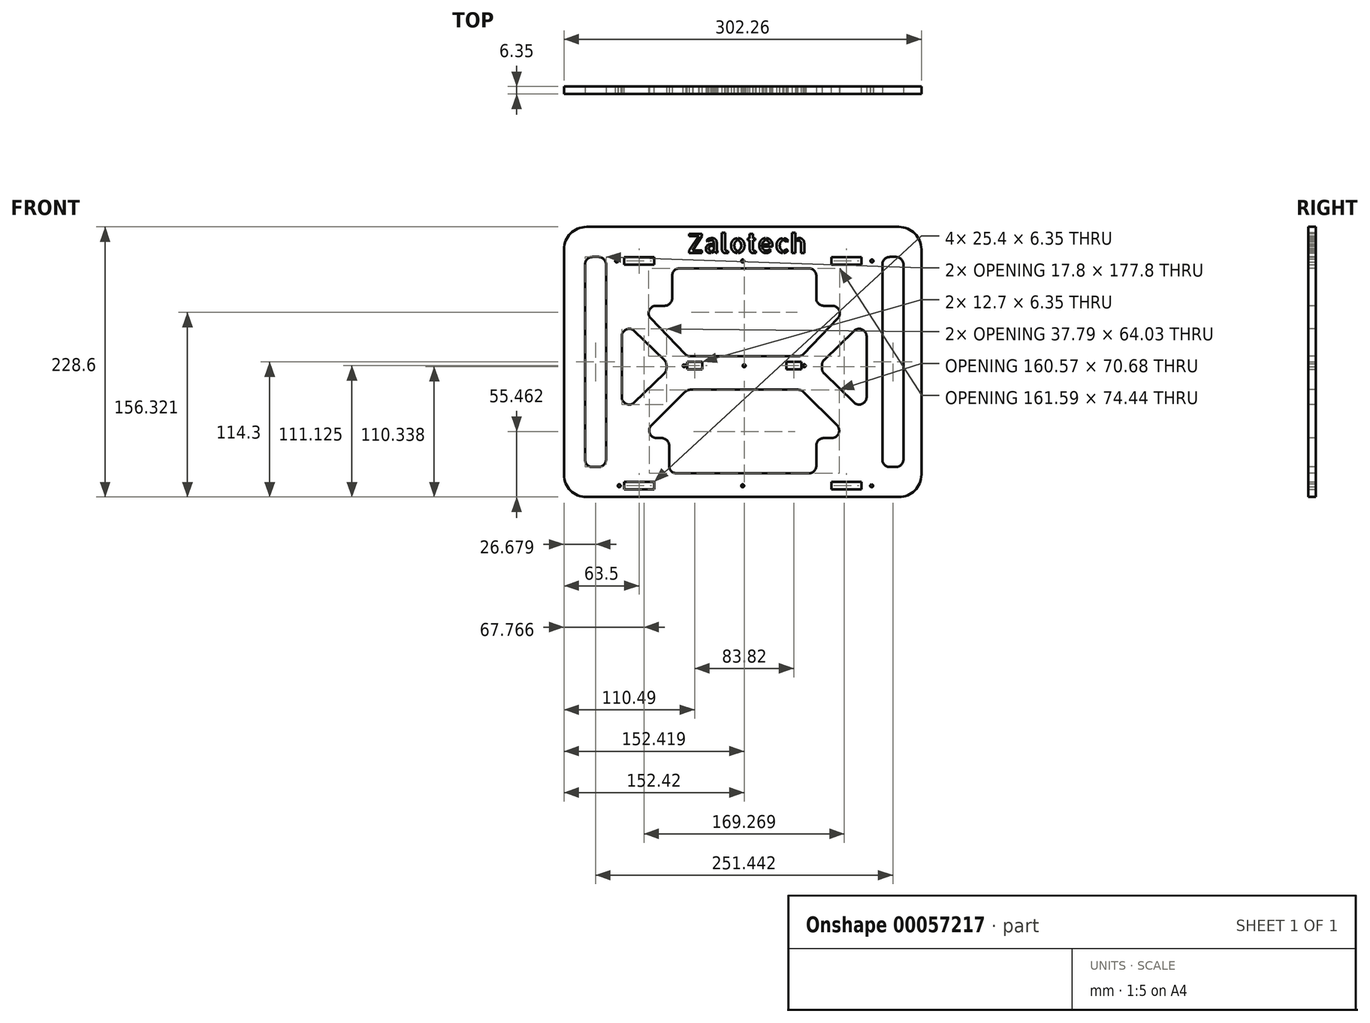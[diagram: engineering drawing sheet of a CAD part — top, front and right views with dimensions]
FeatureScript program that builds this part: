
annotation { "Feature Type Name" : "Feature", "Feature Type Description" : "" }
export const myFeature = defineFeature(function(context is Context, id is Id, definition is map)
    precondition{}
    {
        {
            var Q0;
            Q0=qCreatedBy(makeId("Front.planeOp"),FACE);
            var sketch = newSketch(context, id + "F0", { "sketchPlane" : qUnion([Q0])});
            skLineSegment(sketch, "E0.bottom", {"start": v(-133.35, 114.3) * mm, "end": v(130.8, 114.3) * mm});
            skLineSegment(sketch, "E0.top", {"start": v(-133.35, -114.3) * mm, "end": v(130.8, -114.3) * mm});
            skLineSegment(sketch, "E0.left", {"start": v(-152.4, 95.25) * mm, "end": v(-152.4, -95.25) * mm});
            skLineSegment(sketch, "E0.right", {"start": v(149.86, 95.25) * mm, "end": v(149.86, -95.25) * mm});
            skLineSegment(sketch, "E1", {"start": v(-152.4, -101.6) * mm, "end": v(-101.6, -101.6) * mm, "construction": true});
            skLineSegment(sketch, "E2", {"start": v(149.86, -101.6) * mm, "end": v(99.06, -101.6) * mm, "construction": true});
            skLineSegment(sketch, "E3", {"start": v(-101.6, -101.6) * mm, "end": v(-101.6, -114.3) * mm, "construction": true});
            skLineSegment(sketch, "E4", {"start": v(99.06, -101.6) * mm, "end": v(99.06, -114.3) * mm, "construction": true});
            skPoint(sketch, "E5.oppositeSnap0", {"position": v(-101.6, -107.95) * mm});
            skLineSegment(sketch, "E5.bottom", {"start": v(-101.6, -101.6) * mm, "end": v(-76.2, -101.6) * mm});
            skLineSegment(sketch, "E5.top", {"start": v(-101.6, -107.95) * mm, "end": v(-76.2, -107.95) * mm});
            skLineSegment(sketch, "E5.left", {"start": v(-101.6, -101.6) * mm, "end": v(-101.6, -107.95) * mm});
            skLineSegment(sketch, "E5.right", {"start": v(-76.2, -101.6) * mm, "end": v(-76.2, -107.95) * mm});
            skLineSegment(sketch, "E6.bottom", {"start": v(99.06, -101.6) * mm, "end": v(73.66, -101.6) * mm});
            skLineSegment(sketch, "E6.top", {"start": v(99.06, -107.95) * mm, "end": v(73.66, -107.95) * mm});
            skLineSegment(sketch, "E6.left", {"start": v(99.06, -101.6) * mm, "end": v(99.06, -107.95) * mm});
            skLineSegment(sketch, "E6.right", {"start": v(73.66, -101.6) * mm, "end": v(73.66, -107.95) * mm});
            skLineSegment(sketch, "E7", {"start": v(48.26, 0) * mm, "end": v(-48.26, 0) * mm, "construction": true});
            skLineSegment(sketch, "E8.bottom", {"start": v(48.26, 0) * mm, "end": v(35.56, 0) * mm});
            skLineSegment(sketch, "E8.top", {"start": v(48.26, -6.35) * mm, "end": v(35.56, -6.35) * mm});
            skLineSegment(sketch, "E8.left", {"start": v(48.26, 0) * mm, "end": v(48.26, -6.35) * mm});
            skLineSegment(sketch, "E8.right", {"start": v(35.56, 0) * mm, "end": v(35.56, -6.35) * mm});
            skLineSegment(sketch, "E9.bottom", {"start": v(-48.26, 0) * mm, "end": v(-35.56, 0) * mm});
            skLineSegment(sketch, "E9.top", {"start": v(-48.26, -6.35) * mm, "end": v(-35.56, -6.35) * mm});
            skLineSegment(sketch, "E9.left", {"start": v(-48.26, 0) * mm, "end": v(-48.26, -6.35) * mm});
            skLineSegment(sketch, "E9.right", {"start": v(-35.56, 0) * mm, "end": v(-35.56, -6.35) * mm});
            skLineSegment(sketch, "E10", {"start": v(-101.6, -101.6) * mm, "end": v(-101.6, 88.67) * mm, "construction": true});
            skLineSegment(sketch, "E11", {"start": v(-76.2, -101.6) * mm, "end": v(-76.2, 88.67) * mm, "construction": true});
            skLineSegment(sketch, "E12", {"start": v(-101.6, 88.67) * mm, "end": v(-76.2, 88.67) * mm, "construction": true});
            skLineSegment(sketch, "E13", {"start": v(-101.6, 88.67) * mm, "end": v(108.78, 88.67) * mm, "construction": true});
            skLineSegment(sketch, "E14", {"start": v(99.06, -101.6) * mm, "end": v(99.06, 88.67) * mm, "construction": true});
            skLineSegment(sketch, "E15", {"start": v(73.66, -101.6) * mm, "end": v(73.66, 88.67) * mm, "construction": true});
            skLineSegment(sketch, "E16.bottom", {"start": v(-101.6, 88.67) * mm, "end": v(-76.2, 88.67) * mm});
            skLineSegment(sketch, "E16.top", {"start": v(-101.6, 82.32) * mm, "end": v(-76.2, 82.32) * mm});
            skLineSegment(sketch, "E16.left", {"start": v(-101.6, 88.67) * mm, "end": v(-101.6, 82.32) * mm});
            skLineSegment(sketch, "E16.right", {"start": v(-76.2, 88.67) * mm, "end": v(-76.2, 82.32) * mm});
            skLineSegment(sketch, "E17.bottom", {"start": v(73.66, 88.67) * mm, "end": v(99.06, 88.67) * mm});
            skLineSegment(sketch, "E17.top", {"start": v(73.66, 82.32) * mm, "end": v(99.06, 82.32) * mm});
            skLineSegment(sketch, "E17.left", {"start": v(73.66, 88.67) * mm, "end": v(73.66, 82.32) * mm});
            skLineSegment(sketch, "E17.right", {"start": v(99.06, 88.67) * mm, "end": v(99.06, 82.32) * mm});
            skPoint(sketch, "E18.visualSharp", {"position": v(-152.4, 114.3) * mm});
            skArc(sketch, "E18.filletArc", {"start": v(-133.35, 114.3) * mm, "mid": v(-146.82, 108.72) * mm, "end": v(-152.4, 95.25) * mm});
            skPoint(sketch, "E19.visualSharp", {"position": v(149.86, 114.3) * mm});
            skArc(sketch, "E19.filletArc", {"start": v(149.86, 95.25) * mm, "mid": v(144.28, 108.72) * mm, "end": v(130.8, 114.3) * mm});
            skPoint(sketch, "E20.visualSharp", {"position": v(149.86, -114.3) * mm});
            skArc(sketch, "E20.filletArc", {"start": v(130.8, -114.3) * mm, "mid": v(144.28, -108.72) * mm, "end": v(149.86, -95.25) * mm});
            skPoint(sketch, "E21.visualSharp", {"position": v(-152.4, -114.3) * mm});
            skArc(sketch, "E21.filletArc", {"start": v(-152.4, -95.25) * mm, "mid": v(-146.82, -108.72) * mm, "end": v(-133.35, -114.3) * mm});
            skSolve(sketch);
        }
        {
            var Q0;
            Q0=makeQuery(id+"F0.imprint","IMPRINT",FACE,{"disambiguationData":[TD([[makeQuery(id+"F0.imprint","IMPRINT",EDGE,{"derivedFrom":sQuery(id+"F0.wireOp",EDGE,"E0.bottom")}),-1.0]])]});
            extrude(context, id + "F1", {"entities" : qUnion([Q0]), "depth" : 6.35 * mm});
        }
        {
            var Q0;
            Q0=makeQuery(id+"F1.opExtrude","CAP_FACE",FACE,{"disambiguationData":[OSD([sQuery(id+"F0.wireOp",EDGE,"E0.bottom"),sQuery(id+"F0.wireOp",EDGE,"E0.top"),sQuery(id+"F0.wireOp",EDGE,"E0.left"),sQuery(id+"F0.wireOp",EDGE,"E0.right"),sQuery(id+"F0.wireOp",EDGE,"E5.bottom"),sQuery(id+"F0.wireOp",EDGE,"E5.top"),sQuery(id+"F0.wireOp",EDGE,"E5.left"),sQuery(id+"F0.wireOp",EDGE,"E5.right"),sQuery(id+"F0.wireOp",EDGE,"E6.bottom"),sQuery(id+"F0.wireOp",EDGE,"E6.top"),sQuery(id+"F0.wireOp",EDGE,"E6.left"),sQuery(id+"F0.wireOp",EDGE,"E6.right"),sQuery(id+"F0.wireOp",EDGE,"E8.bottom"),sQuery(id+"F0.wireOp",EDGE,"E8.top"),sQuery(id+"F0.wireOp",EDGE,"E8.left"),sQuery(id+"F0.wireOp",EDGE,"E8.right"),sQuery(id+"F0.wireOp",EDGE,"E9.bottom"),sQuery(id+"F0.wireOp",EDGE,"E9.top"),sQuery(id+"F0.wireOp",EDGE,"E9.left"),sQuery(id+"F0.wireOp",EDGE,"E9.right"),sQuery(id+"F0.wireOp",EDGE,"E16.bottom"),sQuery(id+"F0.wireOp",EDGE,"E16.top"),sQuery(id+"F0.wireOp",EDGE,"E16.left"),sQuery(id+"F0.wireOp",EDGE,"E16.right"),sQuery(id+"F0.wireOp",EDGE,"E17.bottom"),sQuery(id+"F0.wireOp",EDGE,"E17.top"),sQuery(id+"F0.wireOp",EDGE,"E17.left"),sQuery(id+"F0.wireOp",EDGE,"E17.right")])],"isStart":false});
            var sketch = newSketch(context, id + "F2", { "sketchPlane" : qUnion([Q0])});
            skLineSegment(sketch, "E22", {"start": v(-63.5, -77.67) * mm, "end": v(-63.5, -87.83) * mm});
            skLineSegment(sketch, "E23", {"start": v(-57.15, -94.18) * mm, "end": v(54.6, -94.18) * mm});
            skLineSegment(sketch, "E24", {"start": v(60.96, -87.83) * mm, "end": v(60.96, -77.67) * mm});
            skLineSegment(sketch, "E25", {"start": v(-54.6, 79.24) * mm, "end": v(54.6, 79.24) * mm});
            skLineSegment(sketch, "E26", {"start": v(-45.5, 4.8) * mm, "end": v(45.66, 4.8) * mm});
            skLineSegment(sketch, "E27", {"start": v(74.5, 47.62) * mm, "end": v(67.18, 47.62) * mm});
            skLineSegment(sketch, "E28.MirrorCS", {"start": v(-74.47, 47.62) * mm, "end": v(-67.18, 47.62) * mm});
            skLineSegment(sketch, "E29", {"start": v(-50.09, 6.75) * mm, "end": v(-79.04, 36.87) * mm});
            skLineSegment(sketch, "E30", {"start": v(50.24, 6.76) * mm, "end": v(79.1, 36.88) * mm});
            skLineSegment(sketch, "E31", {"start": v(-60.96, 53.84) * mm, "end": v(-60.96, 72.9) * mm});
            skLineSegment(sketch, "E32", {"start": v(60.96, 53.84) * mm, "end": v(60.96, 72.9) * mm});
            skLineSegment(sketch, "E33", {"start": v(-45.5, -23.5) * mm, "end": v(45.66, -23.5) * mm});
            skLineSegment(sketch, "E34", {"start": v(89.38, 47.62) * mm, "end": v(89.38, -82.33) * mm, "construction": true});
            skLineSegment(sketch, "E35", {"start": v(60.96, 47.62) * mm, "end": v(-60.96, 47.62) * mm, "construction": true});
            skLineSegment(sketch, "E36", {"start": v(-78.41, -53.5) * mm, "end": v(-49.98, -25.33) * mm});
            skLineSegment(sketch, "E37", {"start": v(50.14, -25.34) * mm, "end": v(78.46, -53.51) * mm});
            skLineSegment(sketch, "E38", {"start": v(-63.5, -77.67) * mm, "end": v(-63.5, -70.71) * mm});
            skLineSegment(sketch, "E39", {"start": v(60.96, -77.67) * mm, "end": v(60.96, -70.71) * mm});
            skLineSegment(sketch, "E40", {"start": v(73.99, -64.36) * mm, "end": v(67.3, -64.36) * mm});
            skLineSegment(sketch, "E41", {"start": v(-69.85, -64.36) * mm, "end": v(-73.95, -64.36) * mm});
            skArc(sketch, "E42.filletArc", {"start": v(-74.47, 47.62) * mm, "mid": v(-80.3, 43.76) * mm, "end": v(-79.04, 36.87) * mm});
            skPoint(sketch, "E43.visualSharp", {"position": v(89.38, 47.62) * mm});
            skArc(sketch, "E43.filletArc", {"start": v(79.1, 36.88) * mm, "mid": v(80.34, 43.76) * mm, "end": v(74.5, 47.62) * mm});
            skPoint(sketch, "E44.visualSharp", {"position": v(48.37, 4.8) * mm});
            skArc(sketch, "E44.filletArc", {"start": v(45.66, 4.8) * mm, "mid": v(48.15, 5.3) * mm, "end": v(50.24, 6.76) * mm});
            skPoint(sketch, "E45.visualSharp", {"position": v(-48.21, 4.8) * mm});
            skArc(sketch, "E45.filletArc", {"start": v(-50.09, 6.75) * mm, "mid": v(-48, 5.3) * mm, "end": v(-45.5, 4.8) * mm});
            skPoint(sketch, "E46.visualSharp", {"position": v(-48.12, -23.5) * mm});
            skArc(sketch, "E46.filletArc", {"start": v(-45.5, -23.5) * mm, "mid": v(-47.92, -23.97) * mm, "end": v(-49.98, -25.33) * mm});
            skPoint(sketch, "E47.visualSharp", {"position": v(48.28, -23.5) * mm});
            skArc(sketch, "E47.filletArc", {"start": v(50.14, -25.34) * mm, "mid": v(48.08, -23.97) * mm, "end": v(45.66, -23.5) * mm});
            skPoint(sketch, "E48.visualSharp", {"position": v(89.38, -64.36) * mm});
            skArc(sketch, "E48.filletArc", {"start": v(73.99, -64.36) * mm, "mid": v(79.86, -60.44) * mm, "end": v(78.46, -53.51) * mm});
            skArc(sketch, "E49.filletArc", {"start": v(-78.41, -53.5) * mm, "mid": v(-79.82, -60.43) * mm, "end": v(-73.95, -64.36) * mm});
            skPoint(sketch, "E50.visualSharp", {"position": v(-63.5, -64.36) * mm});
            skArc(sketch, "E50.filletArc", {"start": v(-63.5, -70.71) * mm, "mid": v(-65.36, -66.22) * mm, "end": v(-69.85, -64.36) * mm});
            skPoint(sketch, "E51.visualSharp", {"position": v(60.96, -64.36) * mm});
            skArc(sketch, "E51.filletArc", {"start": v(67.3, -64.36) * mm, "mid": v(62.82, -66.22) * mm, "end": v(60.96, -70.71) * mm});
            skArc(sketch, "E52.filletArc", {"start": v(-67.18, 47.62) * mm, "mid": v(-62.78, 49.44) * mm, "end": v(-60.96, 53.84) * mm});
            skArc(sketch, "E53.filletArc", {"start": v(60.96, 53.84) * mm, "mid": v(62.78, 49.44) * mm, "end": v(67.18, 47.62) * mm});
            skArc(sketch, "E54.filletArc", {"start": v(-54.6, 79.24) * mm, "mid": v(-59.1, 77.38) * mm, "end": v(-60.96, 72.9) * mm});
            skArc(sketch, "E55.filletArc", {"start": v(60.96, 72.9) * mm, "mid": v(59.1, 77.38) * mm, "end": v(54.6, 79.24) * mm});
            skPoint(sketch, "E56.visualSharp", {"position": v(-63.5, -94.18) * mm});
            skArc(sketch, "E56.filletArc", {"start": v(-63.5, -87.83) * mm, "mid": v(-61.64, -92.32) * mm, "end": v(-57.15, -94.18) * mm});
            skPoint(sketch, "E57.visualSharp", {"position": v(60.96, -94.18) * mm});
            skArc(sketch, "E57.filletArc", {"start": v(54.6, -94.18) * mm, "mid": v(59.1, -92.32) * mm, "end": v(60.96, -87.83) * mm});
            skSolve(sketch);
        }
        {
            var Q0;
            Q0=makeQuery(id+"F2.imprint","IMPRINT",FACE,{"disambiguationData":[TD([[makeQuery(id+"F2.imprint","IMPRINT",EDGE,{"derivedFrom":sQuery(id+"F2.wireOp",EDGE,"E26")}),1.0]])]});
            var Q1;
            {var subQ3=sQuery(id+"F2.wireOp",EDGE,"E23");Q1=makeQuery(id+"F2.imprint","IMPRINT",FACE,{"disambiguationData":[TD([[makeQuery(id+"F2.imprint","IMPRINT",EDGE,{"derivedFrom":subQ3}),1.0]])]});}
            var Q2;
            Q2=makeQuery(id+"F2.imprint","IMPRINT",FACE,{"disambiguationData":[TD([[makeQuery(id+"F2.imprint","IMPRINT",EDGE,{"derivedFrom":sQuery(id+"F2.wireOp",EDGE,"f44173c2-0543-4982-a62a-dc314a2ca8c5")}),-1.0]])]});
            var Q3;
            Q3=makeQuery(id+"F2.imprint","IMPRINT",FACE,{"disambiguationData":[TD([[makeQuery(id+"F2.imprint","IMPRINT",EDGE,{"derivedFrom":sQuery(id+"F2.wireOp",EDGE,"1ee7fdb6-237e-4fa8-abf3-a4b38ba9088a0.MirrorCS")}),1.0]])]});
            extrude(context, id + "F3", {"entities" : qUnion([Q0, Q1, Q2, Q3]), "operationType" : NewBodyOperationType.REMOVE, "oppositeDirection" : true, "depth" : 25.4 * mm});
        }
        {
            var Q0;
            Q0=makeQuery(id+"F1.opExtrude","CAP_FACE",FACE,{"disambiguationData":[OSD([sQuery(id+"F0.wireOp",EDGE,"E0.bottom"),sQuery(id+"F0.wireOp",EDGE,"E0.top"),sQuery(id+"F0.wireOp",EDGE,"E0.left"),sQuery(id+"F0.wireOp",EDGE,"E0.right"),sQuery(id+"F0.wireOp",EDGE,"E5.bottom"),sQuery(id+"F0.wireOp",EDGE,"E5.top"),sQuery(id+"F0.wireOp",EDGE,"E5.left"),sQuery(id+"F0.wireOp",EDGE,"E5.right"),sQuery(id+"F0.wireOp",EDGE,"E6.bottom"),sQuery(id+"F0.wireOp",EDGE,"E6.top"),sQuery(id+"F0.wireOp",EDGE,"E6.left"),sQuery(id+"F0.wireOp",EDGE,"E6.right"),sQuery(id+"F0.wireOp",EDGE,"E8.bottom"),sQuery(id+"F0.wireOp",EDGE,"E8.top"),sQuery(id+"F0.wireOp",EDGE,"E8.left"),sQuery(id+"F0.wireOp",EDGE,"E8.right"),sQuery(id+"F0.wireOp",EDGE,"E9.bottom"),sQuery(id+"F0.wireOp",EDGE,"E9.top"),sQuery(id+"F0.wireOp",EDGE,"E9.left"),sQuery(id+"F0.wireOp",EDGE,"E9.right"),sQuery(id+"F0.wireOp",EDGE,"E16.bottom"),sQuery(id+"F0.wireOp",EDGE,"E16.top"),sQuery(id+"F0.wireOp",EDGE,"E16.left"),sQuery(id+"F0.wireOp",EDGE,"E16.right"),sQuery(id+"F0.wireOp",EDGE,"E17.bottom"),sQuery(id+"F0.wireOp",EDGE,"E17.top"),sQuery(id+"F0.wireOp",EDGE,"E17.left"),sQuery(id+"F0.wireOp",EDGE,"E17.right"),sQuery(id+"F0.wireOp",EDGE,"E18.filletArc"),sQuery(id+"F0.wireOp",EDGE,"E19.filletArc"),sQuery(id+"F0.wireOp",EDGE,"E20.filletArc"),sQuery(id+"F0.wireOp",EDGE,"E21.filletArc")])],"isStart":false});
            var sketch = newSketch(context, id + "F4", { "sketchPlane" : qUnion([Q0])});
            skLineSegment(sketch, "E58", {"start": v(134.62, 82.55) * mm, "end": v(134.62, -82.55) * mm});
            skLineSegment(sketch, "E59.MirrorCS", {"start": v(-134.62, 88.9) * mm, "end": v(-134.62, -88.9) * mm});
            skLineSegment(sketch, "E60.bottom", {"start": v(-128.27, -88.9) * mm, "end": v(-123.17, -88.9) * mm});
            skLineSegment(sketch, "E60.top", {"start": v(-128.27, 88.9) * mm, "end": v(-123.17, 88.9) * mm});
            skLineSegment(sketch, "E60.left", {"start": v(-134.62, -82.55) * mm, "end": v(-134.62, 82.55) * mm});
            skLineSegment(sketch, "E60.right", {"start": v(-116.82, -82.55) * mm, "end": v(-116.82, 82.55) * mm});
            skLineSegment(sketch, "E61.MirrorCS", {"start": v(116.82, -82.55) * mm, "end": v(116.82, 82.55) * mm});
            skLineSegment(sketch, "E62.MirrorCS", {"start": v(128.27, 88.9) * mm, "end": v(123.17, 88.9) * mm});
            skLineSegment(sketch, "E63.MirrorCS", {"start": v(128.27, -88.9) * mm, "end": v(123.17, -88.9) * mm});
            skPoint(sketch, "E64.visualSharp", {"position": v(-116.82, 88.9) * mm});
            skArc(sketch, "E64.filletArc", {"start": v(-116.82, 82.55) * mm, "mid": v(-118.68, 87.04) * mm, "end": v(-123.17, 88.9) * mm});
            skPoint(sketch, "E65.visualSharp", {"position": v(-134.62, 88.9) * mm});
            skArc(sketch, "E65.filletArc", {"start": v(-128.27, 88.9) * mm, "mid": v(-132.76, 87.04) * mm, "end": v(-134.62, 82.55) * mm});
            skPoint(sketch, "E66.visualSharp", {"position": v(-116.82, -88.9) * mm});
            skArc(sketch, "E66.filletArc", {"start": v(-123.17, -88.9) * mm, "mid": v(-118.68, -87.04) * mm, "end": v(-116.82, -82.55) * mm});
            skPoint(sketch, "E67.visualSharp", {"position": v(-134.62, -88.9) * mm});
            skArc(sketch, "E67.filletArc", {"start": v(-134.62, -82.55) * mm, "mid": v(-132.76, -87.04) * mm, "end": v(-128.27, -88.9) * mm});
            skPoint(sketch, "E68.visualSharp", {"position": v(116.82, -88.9) * mm});
            skArc(sketch, "E68.filletArc", {"start": v(116.82, -82.55) * mm, "mid": v(118.68, -87.04) * mm, "end": v(123.17, -88.9) * mm});
            skPoint(sketch, "E69.visualSharp", {"position": v(134.62, -88.9) * mm});
            skArc(sketch, "E69.filletArc", {"start": v(128.27, -88.9) * mm, "mid": v(132.76, -87.04) * mm, "end": v(134.62, -82.55) * mm});
            skPoint(sketch, "E70.visualSharp", {"position": v(134.62, 88.9) * mm});
            skArc(sketch, "E70.filletArc", {"start": v(134.62, 82.55) * mm, "mid": v(132.76, 87.04) * mm, "end": v(128.27, 88.9) * mm});
            skPoint(sketch, "E71.visualSharp", {"position": v(116.82, 88.9) * mm});
            skArc(sketch, "E71.filletArc", {"start": v(123.17, 88.9) * mm, "mid": v(118.68, 87.04) * mm, "end": v(116.82, 82.55) * mm});
            skSolve(sketch);
        }
        {
            var Q0;
            Q0=qSketchRegion(id+"F4",true);
            extrude(context, id + "F5", {"entities" : qUnion([Q0]), "operationType" : NewBodyOperationType.REMOVE, "oppositeDirection" : true, "depth" : 25.4 * mm});
        }
        {
            var Q0;
            {var subQ3=sQuery(id+"F4.wireOp",EDGE,"E62.MirrorCS");Q0=makeQuery(id+"F4.imprint","IMPRINT",FACE,{"disambiguationData":[TD([[makeQuery(id+"F4.imprint","IMPRINT",EDGE,{"derivedFrom":subQ3}),1.0]])]});}
            var Q1;
            {var subQ3=sQuery(id+"F4.wireOp",EDGE,"E63.MirrorCS");Q1=makeQuery(id+"F4.imprint","IMPRINT",FACE,{"disambiguationData":[TD([[makeQuery(id+"F4.imprint","IMPRINT",EDGE,{"derivedFrom":subQ3}),-1.0]])]});}
            var Q2;
            {var subQ0=sQuery(id+"F4.wireOp",EDGE,"E60.bottom");Q2=makeQuery(id+"F4.imprint","IMPRINT",FACE,{"disambiguationData":[TD([[makeQuery(id+"F4.imprint","IMPRINT",EDGE,{"derivedFrom":subQ0}),1.0]])]});}
            var Q3;
            {var subQ5=sQuery(id+"F4.wireOp",EDGE,"E60.top");Q3=makeQuery(id+"F4.imprint","IMPRINT",FACE,{"disambiguationData":[TD([[makeQuery(id+"F4.imprint","IMPRINT",EDGE,{"derivedFrom":subQ5}),-1.0]])]});}
            extrude(context, id + "F6", {"entities" : qUnion([Q0, Q1, Q2, Q3]), "operationType" : NewBodyOperationType.REMOVE, "oppositeDirection" : true, "depth" : 25.4 * mm});
        }
        {
            var Q0;
            Q0=makeQuery(id+"F1.opExtrude","CAP_FACE",FACE,{"disambiguationData":[OSD([sQuery(id+"F0.wireOp",EDGE,"E0.bottom"),sQuery(id+"F0.wireOp",EDGE,"E0.top"),sQuery(id+"F0.wireOp",EDGE,"E0.left"),sQuery(id+"F0.wireOp",EDGE,"E0.right"),sQuery(id+"F0.wireOp",EDGE,"E5.bottom"),sQuery(id+"F0.wireOp",EDGE,"E5.top"),sQuery(id+"F0.wireOp",EDGE,"E5.left"),sQuery(id+"F0.wireOp",EDGE,"E5.right"),sQuery(id+"F0.wireOp",EDGE,"E6.bottom"),sQuery(id+"F0.wireOp",EDGE,"E6.top"),sQuery(id+"F0.wireOp",EDGE,"E6.left"),sQuery(id+"F0.wireOp",EDGE,"E6.right"),sQuery(id+"F0.wireOp",EDGE,"E8.bottom"),sQuery(id+"F0.wireOp",EDGE,"E8.top"),sQuery(id+"F0.wireOp",EDGE,"E8.left"),sQuery(id+"F0.wireOp",EDGE,"E8.right"),sQuery(id+"F0.wireOp",EDGE,"E9.bottom"),sQuery(id+"F0.wireOp",EDGE,"E9.top"),sQuery(id+"F0.wireOp",EDGE,"E9.left"),sQuery(id+"F0.wireOp",EDGE,"E9.right"),sQuery(id+"F0.wireOp",EDGE,"E16.bottom"),sQuery(id+"F0.wireOp",EDGE,"E16.top"),sQuery(id+"F0.wireOp",EDGE,"E16.left"),sQuery(id+"F0.wireOp",EDGE,"E16.right"),sQuery(id+"F0.wireOp",EDGE,"E17.bottom"),sQuery(id+"F0.wireOp",EDGE,"E17.top"),sQuery(id+"F0.wireOp",EDGE,"E17.left"),sQuery(id+"F0.wireOp",EDGE,"E17.right"),sQuery(id+"F0.wireOp",EDGE,"E18.filletArc"),sQuery(id+"F0.wireOp",EDGE,"E19.filletArc"),sQuery(id+"F0.wireOp",EDGE,"E20.filletArc"),sQuery(id+"F0.wireOp",EDGE,"E21.filletArc")])],"isStart":false});
            var sketch = newSketch(context, id + "F7", { "sketchPlane" : qUnion([Q0])});
            skCircle(sketch, "E72", {"center": v(-50.7, -3.18) * mm, "radius": 1.27 * mm});
            skCircle(sketch, "E73", {"center": v(0, -3.18) * mm, "radius": 1.27 * mm});
            skCircle(sketch, "E74", {"center": v(50.8, -3.18) * mm, "radius": 1.27 * mm});
            skLineSegment(sketch, "E75", {"start": v(-48.26, -3.18) * mm, "end": v(35.56, -3.18) * mm, "construction": true});
            skLineSegment(sketch, "E76", {"start": v(-101.6, 85.5) * mm, "end": v(99.06, 85.5) * mm, "construction": true});
            skCircle(sketch, "E77", {"center": v(-1.27, 85.5) * mm, "radius": 1.27 * mm});
            skCircle(sketch, "E78", {"center": v(-107.77, 85.5) * mm, "radius": 1.27 * mm});
            skCircle(sketch, "E79", {"center": v(108.04, 85.5) * mm, "radius": 1.27 * mm});
            skLineSegment(sketch, "E80", {"start": v(-101.6, -104.78) * mm, "end": v(99.06, -104.78) * mm, "construction": true});
            skCircle(sketch, "E81", {"center": v(-105.65, -104.78) * mm, "radius": 1.27 * mm});
            skCircle(sketch, "E82", {"center": v(-1.27, -104.78) * mm, "radius": 1.27 * mm});
            skCircle(sketch, "E83", {"center": v(107.77, -104.78) * mm, "radius": 1.27 * mm});
            skSolve(sketch);
        }
        {
            var Q0;
            Q0=qSketchRegion(id+"F7",true);
            extrude(context, id + "F8", {"entities" : qUnion([Q0]), "operationType" : NewBodyOperationType.REMOVE, "oppositeDirection" : true, "depth" : 25.4 * mm});
        }
        {
            var Q0;
            Q0=makeQuery(id+"F1.opExtrude","CAP_FACE",FACE,{"disambiguationData":[OSD([sQuery(id+"F0.wireOp",EDGE,"E0.bottom"),sQuery(id+"F0.wireOp",EDGE,"E0.top"),sQuery(id+"F0.wireOp",EDGE,"E0.left"),sQuery(id+"F0.wireOp",EDGE,"E0.right"),sQuery(id+"F0.wireOp",EDGE,"E5.bottom"),sQuery(id+"F0.wireOp",EDGE,"E5.top"),sQuery(id+"F0.wireOp",EDGE,"E5.left"),sQuery(id+"F0.wireOp",EDGE,"E5.right"),sQuery(id+"F0.wireOp",EDGE,"E6.bottom"),sQuery(id+"F0.wireOp",EDGE,"E6.top"),sQuery(id+"F0.wireOp",EDGE,"E6.left"),sQuery(id+"F0.wireOp",EDGE,"E6.right"),sQuery(id+"F0.wireOp",EDGE,"E8.bottom"),sQuery(id+"F0.wireOp",EDGE,"E8.top"),sQuery(id+"F0.wireOp",EDGE,"E8.left"),sQuery(id+"F0.wireOp",EDGE,"E8.right"),sQuery(id+"F0.wireOp",EDGE,"E9.bottom"),sQuery(id+"F0.wireOp",EDGE,"E9.top"),sQuery(id+"F0.wireOp",EDGE,"E9.left"),sQuery(id+"F0.wireOp",EDGE,"E9.right"),sQuery(id+"F0.wireOp",EDGE,"E16.bottom"),sQuery(id+"F0.wireOp",EDGE,"E16.top"),sQuery(id+"F0.wireOp",EDGE,"E16.left"),sQuery(id+"F0.wireOp",EDGE,"E16.right"),sQuery(id+"F0.wireOp",EDGE,"E17.bottom"),sQuery(id+"F0.wireOp",EDGE,"E17.top"),sQuery(id+"F0.wireOp",EDGE,"E17.left"),sQuery(id+"F0.wireOp",EDGE,"E17.right"),sQuery(id+"F0.wireOp",EDGE,"E18.filletArc"),sQuery(id+"F0.wireOp",EDGE,"E19.filletArc"),sQuery(id+"F0.wireOp",EDGE,"E20.filletArc"),sQuery(id+"F0.wireOp",EDGE,"E21.filletArc")])],"isStart":false});
            var sketch = newSketch(context, id + "F9", { "sketchPlane" : qUnion([Q0])});
            skLineSegment(sketch, "E84", {"start": v(-65.74, -3.18) * mm, "end": v(-65.74, -2.68) * mm});
            skPoint(sketch, "E84.startSnap0", {"position": v(-48.26, -3.18) * mm});
            skLineSegment(sketch, "E85", {"start": v(-65.74, -3.18) * mm, "end": v(-65.74, -5.24) * mm});
            skLineSegment(sketch, "E86", {"start": v(-67.66, -9.8) * mm, "end": v(-92.75, -34.21) * mm});
            skLineSegment(sketch, "E87", {"start": v(-103.53, -29.66) * mm, "end": v(-103.53, 21.74) * mm});
            skLineSegment(sketch, "E88", {"start": v(-67.66, 1.87) * mm, "end": v(-92.75, 26.29) * mm});
            skLineSegment(sketch, "E89.MirrorCS", {"start": v(65.74, -3.18) * mm, "end": v(65.74, -2.68) * mm});
            skLineSegment(sketch, "E90.MirrorCS", {"start": v(65.74, -3.18) * mm, "end": v(65.74, -5.24) * mm});
            skLineSegment(sketch, "E91.MirrorCS", {"start": v(67.66, 1.87) * mm, "end": v(92.75, 26.29) * mm});
            skLineSegment(sketch, "E92.MirrorCS", {"start": v(103.53, -29.66) * mm, "end": v(103.53, 21.74) * mm});
            skLineSegment(sketch, "E93.MirrorCS", {"start": v(67.66, -9.8) * mm, "end": v(92.75, -34.21) * mm});
            skPoint(sketch, "E94.visualSharp", {"position": v(-103.53, 36.78) * mm});
            skArc(sketch, "E94.filletArc", {"start": v(-92.75, 26.29) * mm, "mid": v(-99.65, 27.59) * mm, "end": v(-103.53, 21.74) * mm});
            skPoint(sketch, "E95.visualSharp", {"position": v(-103.53, -44.7) * mm});
            skArc(sketch, "E95.filletArc", {"start": v(-103.53, -29.66) * mm, "mid": v(-99.65, -35.51) * mm, "end": v(-92.75, -34.21) * mm});
            skPoint(sketch, "E96.visualSharp", {"position": v(-65.74, -7.92) * mm});
            skArc(sketch, "E96.filletArc", {"start": v(-67.66, -9.8) * mm, "mid": v(-66.24, -7.71) * mm, "end": v(-65.74, -5.24) * mm});
            skPoint(sketch, "E97.visualSharp", {"position": v(-65.74, 0) * mm});
            skArc(sketch, "E97.filletArc", {"start": v(-65.74, -2.68) * mm, "mid": v(-66.24, -0.21) * mm, "end": v(-67.66, 1.87) * mm});
            skPoint(sketch, "E98.visualSharp", {"position": v(65.74, -7.92) * mm});
            skArc(sketch, "E98.filletArc", {"start": v(65.74, -5.24) * mm, "mid": v(66.24, -7.71) * mm, "end": v(67.66, -9.8) * mm});
            skPoint(sketch, "E99.visualSharp", {"position": v(65.74, 0) * mm});
            skArc(sketch, "E99.filletArc", {"start": v(67.66, 1.87) * mm, "mid": v(66.24, -0.21) * mm, "end": v(65.74, -2.68) * mm});
            skPoint(sketch, "E100.visualSharp", {"position": v(103.53, 36.78) * mm});
            skArc(sketch, "E100.filletArc", {"start": v(103.53, 21.74) * mm, "mid": v(99.65, 27.59) * mm, "end": v(92.75, 26.29) * mm});
            skPoint(sketch, "E101.visualSharp", {"position": v(103.53, -44.7) * mm});
            skArc(sketch, "E101.filletArc", {"start": v(92.75, -34.21) * mm, "mid": v(99.65, -35.51) * mm, "end": v(103.53, -29.66) * mm});
            skSolve(sketch);
        }
        {
            var Q0;
            Q0=makeQuery(id+"F9.imprint","IMPRINT",FACE,{"disambiguationData":[TD([[makeQuery(id+"F9.imprint","IMPRINT",EDGE,{"derivedFrom":sQuery(id+"F9.wireOp",EDGE,"E84")}),1.0]])]});
            var Q1;
            Q1=makeQuery(id+"F9.imprint","IMPRINT",FACE,{"disambiguationData":[TD([[makeQuery(id+"F9.imprint","IMPRINT",EDGE,{"derivedFrom":sQuery(id+"F9.wireOp",EDGE,"E89.MirrorCS")}),-1.0]])]});
            extrude(context, id + "F10", {"entities" : qUnion([Q0, Q1]), "operationType" : NewBodyOperationType.REMOVE, "oppositeDirection" : true, "depth" : 25.4 * mm});
        }
        {
            var Q0;
            Q0=makeQuery(id+"F1.opExtrude","CAP_FACE",FACE,{"disambiguationData":[OSD([sQuery(id+"F0.wireOp",EDGE,"E0.bottom"),sQuery(id+"F0.wireOp",EDGE,"E0.top"),sQuery(id+"F0.wireOp",EDGE,"E0.left"),sQuery(id+"F0.wireOp",EDGE,"E0.right"),sQuery(id+"F0.wireOp",EDGE,"E5.bottom"),sQuery(id+"F0.wireOp",EDGE,"E5.top"),sQuery(id+"F0.wireOp",EDGE,"E5.left"),sQuery(id+"F0.wireOp",EDGE,"E5.right"),sQuery(id+"F0.wireOp",EDGE,"E6.bottom"),sQuery(id+"F0.wireOp",EDGE,"E6.top"),sQuery(id+"F0.wireOp",EDGE,"E6.left"),sQuery(id+"F0.wireOp",EDGE,"E6.right"),sQuery(id+"F0.wireOp",EDGE,"E8.bottom"),sQuery(id+"F0.wireOp",EDGE,"E8.top"),sQuery(id+"F0.wireOp",EDGE,"E8.left"),sQuery(id+"F0.wireOp",EDGE,"E8.right"),sQuery(id+"F0.wireOp",EDGE,"E9.bottom"),sQuery(id+"F0.wireOp",EDGE,"E9.top"),sQuery(id+"F0.wireOp",EDGE,"E9.left"),sQuery(id+"F0.wireOp",EDGE,"E9.right"),sQuery(id+"F0.wireOp",EDGE,"E16.bottom"),sQuery(id+"F0.wireOp",EDGE,"E16.top"),sQuery(id+"F0.wireOp",EDGE,"E16.left"),sQuery(id+"F0.wireOp",EDGE,"E16.right"),sQuery(id+"F0.wireOp",EDGE,"E17.bottom"),sQuery(id+"F0.wireOp",EDGE,"E17.top"),sQuery(id+"F0.wireOp",EDGE,"E17.left"),sQuery(id+"F0.wireOp",EDGE,"E17.right"),sQuery(id+"F0.wireOp",EDGE,"E18.filletArc"),sQuery(id+"F0.wireOp",EDGE,"E19.filletArc"),sQuery(id+"F0.wireOp",EDGE,"E20.filletArc"),sQuery(id+"F0.wireOp",EDGE,"E21.filletArc")])],"isStart":false});
            var sketch = newSketch(context, id + "F11", { "sketchPlane" : qUnion([Q0])});
            skText(sketch, "E102", { "text": "Zalotech", "fontName": "AllertaStencil-Regular.ttf"});
            const initialGuessF11  = {"E102": [-0.04819, 0.0923, 1, 0, 0.01626]};
            skSetInitialGuess(sketch, initialGuessF11);
            skSolve(sketch);
        }
        {
            var Q0;
            Q0=qSketchRegion(id+"F11",true);
            extrude(context, id + "F12", {"entities" : qUnion([Q0]), "operationType" : NewBodyOperationType.REMOVE, "oppositeDirection" : true, "depth" : 25.4 * mm});
        }
    });
